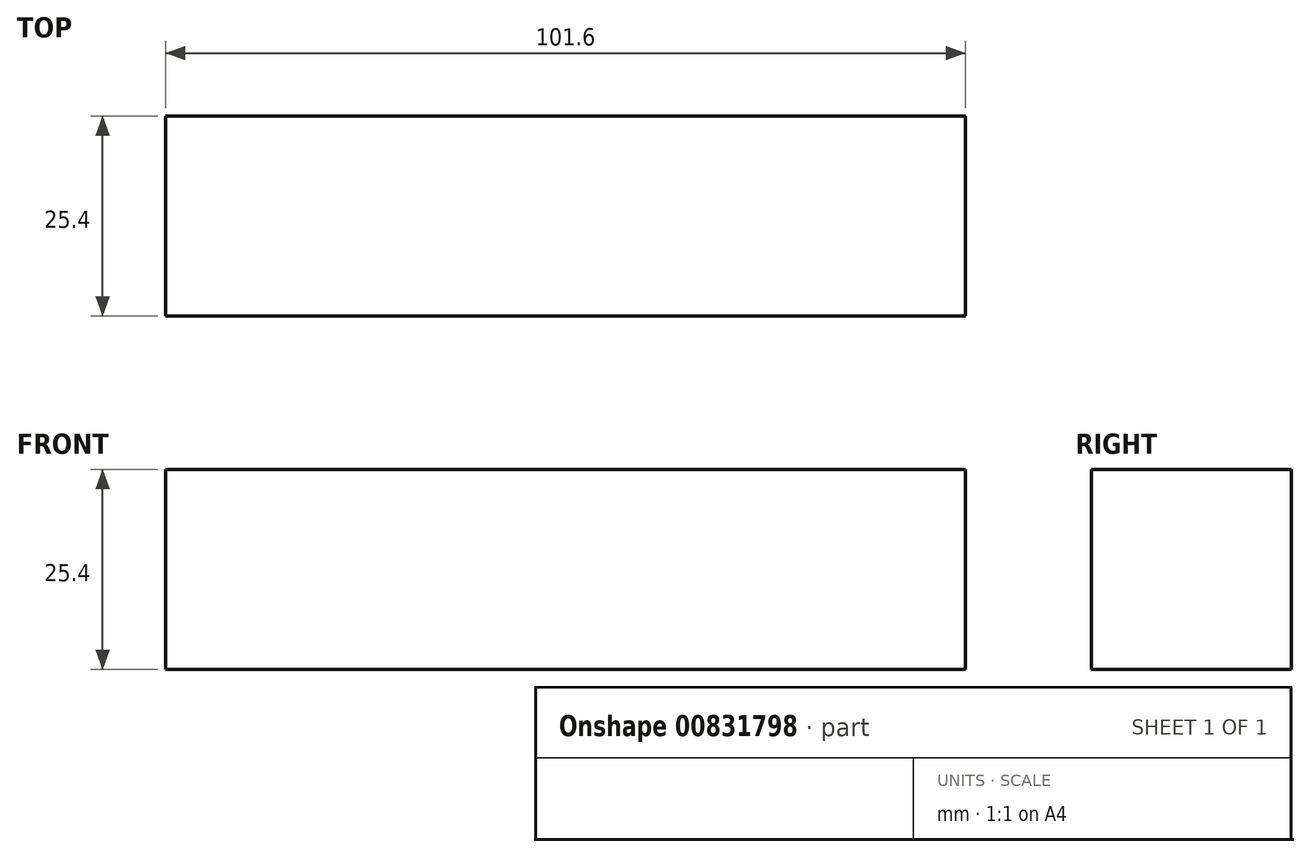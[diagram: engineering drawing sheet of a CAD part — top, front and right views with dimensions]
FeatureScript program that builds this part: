
annotation { "Feature Type Name" : "Feature", "Feature Type Description" : "" }
export const myFeature = defineFeature(function(context is Context, id is Id, definition is map)
    precondition{}
    {
        {
            var Q0;
            Q0=qCreatedBy(makeId("Front.planeOp"),FACE);
            var sketch = newSketch(context, id + "F0", { "sketchPlane" : qUnion([Q0])});
            skLineSegment(sketch, "E0.bottom", {"start": v(-101.6, 51.09) * mm, "end": v(0, 51.09) * mm});
            skLineSegment(sketch, "E0.top", {"start": v(-101.6, 25.69) * mm, "end": v(0, 25.69) * mm});
            skLineSegment(sketch, "E0.left", {"start": v(-101.6, 51.09) * mm, "end": v(-101.6, 25.69) * mm});
            skLineSegment(sketch, "E0.right", {"start": v(0, 51.09) * mm, "end": v(0, 25.69) * mm});
            skSolve(sketch);
        }
        {
            var Q0;
            Q0 = qSketchRegion(id + "F0", true);
            extrude(context, id + "F1", {"entities" : qUnion([Q0]), "depth" : 25.4 * mm, "offsetDistance" : 25.4 * mm});
        }
    });
